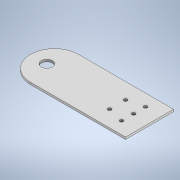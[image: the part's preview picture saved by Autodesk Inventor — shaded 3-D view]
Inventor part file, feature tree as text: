
AUTODESK INVENTOR PART (.ipt)
format: ipt  version: 2022 (Build 260153000, 153)  size: 135,680 bytes
history: native  units: mm
features: sheet_metal_op x1, sketch x1, other x1
ambient origin geometry x8: Origin, YZ Plane, XZ Plane, XY Plane, X Axis, Y Axis, Z Axis, Center Point
bodies: Body1 (feature_tree)
feature tree (3):
  sheet_metal_op  "Face3"
  sketch  "Sketch2"  dims[d36=44.0mm d37=44.0mm d38=65.0mm d41=10.2mm d42=22.0mm d43=15.0mm d44=14.666667mm d45=14.666667mm d46=14.666667mm d47=11.0mm d48=11.0mm d49=11.0mm d50=11.0mm d51=3.25mm d52=3.25mm d53=3.25mm d54=3.25mm d55=3.25mm d56=14.666667mm d57=14.666667mm d58=14.666667mm d59=14.666667mm d60=2.0mm]
  other  "Plate3"
